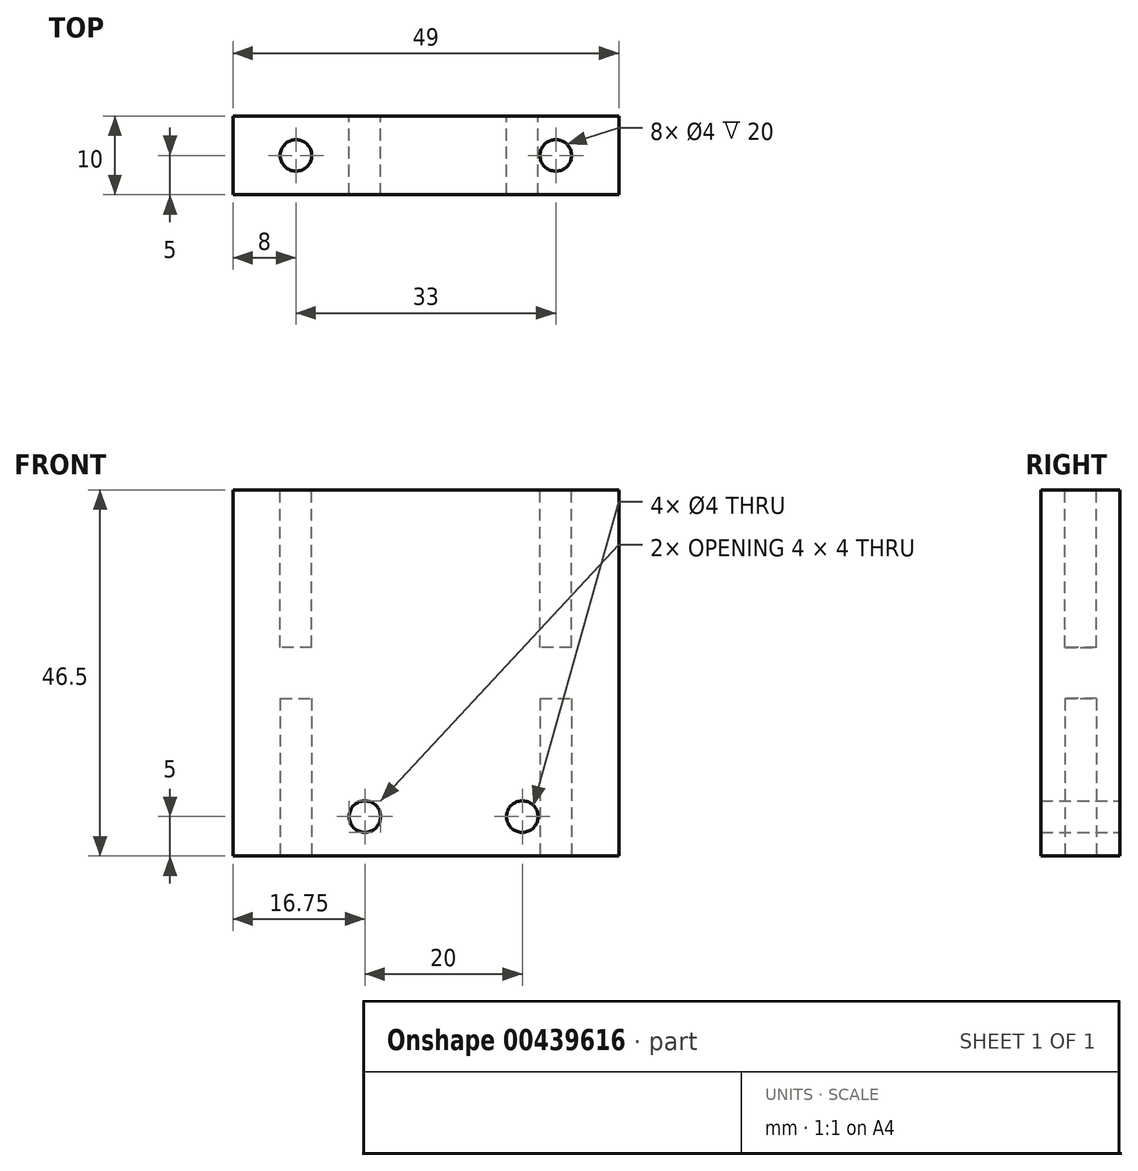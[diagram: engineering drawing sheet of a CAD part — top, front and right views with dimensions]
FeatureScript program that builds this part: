
annotation { "Feature Type Name" : "Feature", "Feature Type Description" : "" }
export const myFeature = defineFeature(function(context is Context, id is Id, definition is map)
    precondition{}
    {
        {
            var Q0;
            Q0=qCreatedBy(makeId("Front.planeOp"),FACE);
            var sketch = newSketch(context, id + "F0", { "sketchPlane" : qUnion([Q0])});
            skLineSegment(sketch, "E0.bottom", {"start": v(-24.5, 0) * mm, "end": v(24.5, 0) * mm});
            skLineSegment(sketch, "E0.top", {"start": v(-24.5, 46.5) * mm, "end": v(24.5, 46.5) * mm});
            skLineSegment(sketch, "E0.left", {"start": v(-24.5, 0) * mm, "end": v(-24.5, 46.5) * mm});
            skLineSegment(sketch, "E0.right", {"start": v(24.5, 0) * mm, "end": v(24.5, 46.5) * mm});
            skSolve(sketch);
        }
        {
            var Q0;
            Q0 = qSketchRegion(id + "F0", true);
            extrude(context, id + "F1", {"entities" : qUnion([Q0]), "depth" : 10 * mm});
        }
        {
            var Q0;
            Q0=makeQuery(id+"F1.opExtrude","CAP_FACE",FACE,{"disambiguationData":[OSD([sQuery(id+"F0.wireOp",EDGE,"E0.bottom"),sQuery(id+"F0.wireOp",EDGE,"E0.top"),sQuery(id+"F0.wireOp",EDGE,"E0.left"),sQuery(id+"F0.wireOp",EDGE,"E0.right")])],"isStart":true});
            var sketch = newSketch(context, id + "F2", { "sketchPlane" : qUnion([Q0])});
            skCircle(sketch, "E1", {"center": v(-12.25, 5) * mm, "radius": 2 * mm});
            skCircle(sketch, "E2.1.0.0", {"center": v(7.75, 5) * mm, "radius": 2 * mm});
            skLineSegment(sketch, "E2.direction1", {"start": v(-12.25, 5) * mm, "end": v(7.75, 5) * mm, "construction": true});
            skSolve(sketch);
        }
        {
            var Q0;
            Q0 = qSketchRegion(id + "F2", true);
            extrude(context, id + "F3", {"entities" : qUnion([Q0]), "operationType" : NewBodyOperationType.REMOVE, "endBound" : BoundingType.THROUGH_ALL, "oppositeDirection" : true, "depth" : 25 * mm});
        }
        {
            var Q0;
            Q0=makeQuery(id+"F1.opExtrude","SWEPT_FACE",FACE,{"disambiguationData":[OSD([sQuery(id+"F0.wireOp",EDGE,"E0.top")])]});
            var sketch = newSketch(context, id + "F4", { "sketchPlane" : qUnion([Q0])});
            skCircle(sketch, "E3", {"center": v(16.5, -5) * mm, "radius": 2 * mm});
            skPoint(sketch, "E3.centerSnap0", {"position": v(-24.5, -5) * mm});
            skCircle(sketch, "E4.1.0.0", {"center": v(-16.5, -5) * mm, "radius": 2 * mm});
            skLineSegment(sketch, "E4.direction1", {"start": v(16.5, -5) * mm, "end": v(-16.5, -5) * mm, "construction": true});
            skSolve(sketch);
        }
        {
            var Q0;
            Q0 = qSketchRegion(id + "F4", true);
            extrude(context, id + "F5", {"entities" : qUnion([Q0]), "operationType" : NewBodyOperationType.REMOVE, "oppositeDirection" : true, "depth" : 20 * mm});
        }
        {
            var Q0;
            Q0=makeQuery(id+"F1.opExtrude","SWEPT_FACE",FACE,{"disambiguationData":[OSD([sQuery(id+"F0.wireOp",EDGE,"E0.bottom")])]});
            var sketch = newSketch(context, id + "F6", { "sketchPlane" : qUnion([Q0])});
            skCircle(sketch, "E5", {"center": v(-16.5, 5) * mm, "radius": 2 * mm});
            skPoint(sketch, "E5.centerSnap0", {"position": v(-24.5, 5) * mm});
            skCircle(sketch, "E6", {"center": v(16.5, 5) * mm, "radius": 2 * mm});
            skSolve(sketch);
        }
        {
            var Q0;
            Q0 = qSketchRegion(id + "F6", true);
            extrude(context, id + "F7", {"entities" : qUnion([Q0]), "operationType" : NewBodyOperationType.REMOVE, "oppositeDirection" : true, "depth" : 20 * mm});
        }
    });
